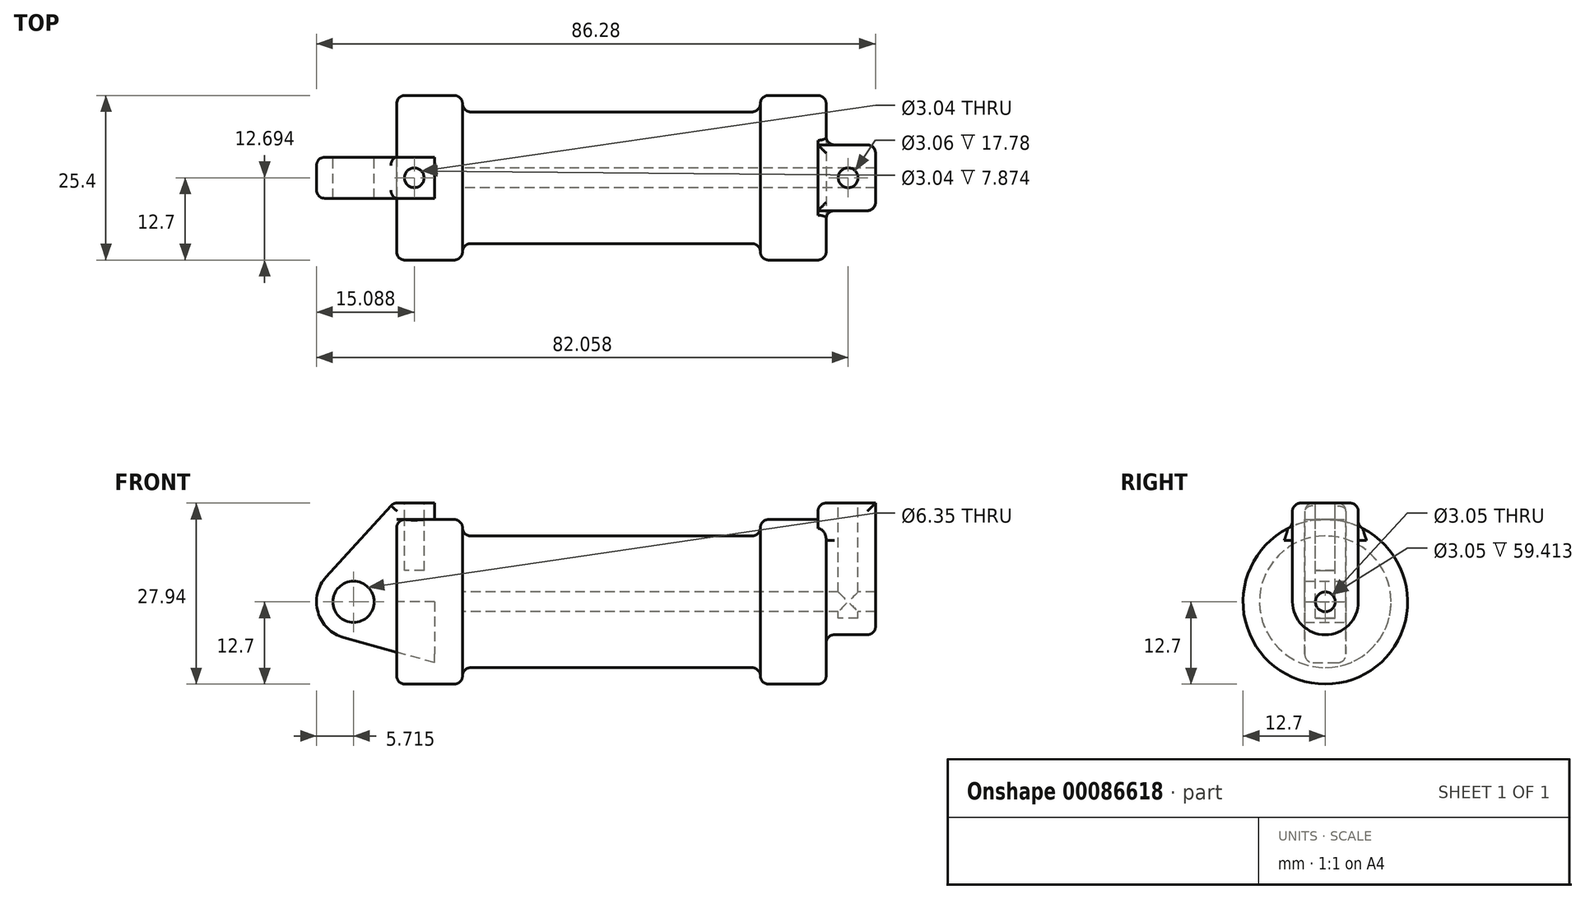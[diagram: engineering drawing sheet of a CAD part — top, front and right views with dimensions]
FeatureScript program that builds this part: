
annotation { "Feature Type Name" : "Feature", "Feature Type Description" : "" }
export const myFeature = defineFeature(function(context is Context, id is Id, definition is map)
    precondition{}
    {
        {
            var Q0;
            Q0=qCreatedBy(makeId("Front.planeOp"),FACE);
            var sketch = newSketch(context, id + "F0", { "sketchPlane" : qUnion([Q0])});
            skLineSegment(sketch, "E0", {"start": v(0, 0) * mm, "end": v(0, 12.7) * mm});
            skLineSegment(sketch, "E1", {"start": v(0, 12.7) * mm, "end": v(10.16, 12.7) * mm});
            skLineSegment(sketch, "E2", {"start": v(10.16, 12.7) * mm, "end": v(10.16, 10.16) * mm});
            skLineSegment(sketch, "E3", {"start": v(10.16, 10.16) * mm, "end": v(56.13, 10.16) * mm});
            skLineSegment(sketch, "E4", {"start": v(56.13, 10.16) * mm, "end": v(56.13, 12.7) * mm});
            skLineSegment(sketch, "E5", {"start": v(56.13, 12.7) * mm, "end": v(66.3, 12.7) * mm});
            skLineSegment(sketch, "E6", {"start": v(66.3, 12.7) * mm, "end": v(66.3, 0) * mm});
            skLineSegment(sketch, "E7", {"start": v(66.3, 0) * mm, "end": v(0, 0) * mm});
            skLineSegment(sketch, "E8", {"start": v(5.84, 15.24) * mm, "end": v(-0.5, 15.24) * mm});
            skLineSegment(sketch, "E9", {"start": v(-0.5, 15.24) * mm, "end": v(-10.88, 3.85) * mm});
            skLineSegment(sketch, "E10", {"start": v(0, 0) * mm, "end": v(-6.65, 0) * mm});
            skCircle(sketch, "E11", {"center": v(-6.65, 0) * mm, "radius": 5.72 * mm});
            skCircle(sketch, "E12", {"center": v(-6.65, 0) * mm, "radius": 3.18 * mm});
            skLineSegment(sketch, "E13", {"start": v(5.84, 15.24) * mm, "end": v(5.84, -9.4) * mm});
            skLineSegment(sketch, "E14", {"start": v(5.84, -9.4) * mm, "end": v(-8.18, -5.5) * mm});
            skSolve(sketch);
        }
        {
            var Q0;
            {var subQ0=sQuery(id+"F0.wireOp",EDGE,"E2");Q0=makeQuery(id+"F0.imprint","IMPRINT",FACE,{"disambiguationData":[TD([[makeQuery(id+"F0.imprint","IMPRINT",EDGE,{"derivedFrom":subQ0}),-1.0]])]});}
            var Q1;
            {var subQ0=sQuery(id+"F0.wireOp",EDGE,"E0");Q1=makeQuery(id+"F0.imprint","IMPRINT",FACE,{"disambiguationData":[TD([[makeQuery(id+"F0.imprint","IMPRINT",EDGE,{"derivedFrom":subQ0}),-1.0]])]});}
            var Q2;
            Q2=sQuery(id+"F0.wireOp",EDGE,"E7");
            revolve(context, id + "F1", {"entities" : qUnion([Q0, Q1]), "axis" : qUnion([Q2]), "revolveType" : RevolveType.FULL});
        }
        {
            var Q0;
            {var subQ3=sQuery(id+"F0.wireOp",EDGE,"E0");Q0=makeQuery(id+"F0.imprint","IMPRINT",FACE,{"disambiguationData":[TD([[makeQuery(id+"F0.imprint","IMPRINT",EDGE,{"derivedFrom":subQ3}),1.0]])]});}
            var Q1;
            {var subQ4=sQuery(id+"F0.wireOp",EDGE,"E12");Q1=makeQuery(id+"F0.imprint","IMPRINT",FACE,{"disambiguationData":[TD([[makeQuery(id+"F0.imprint","IMPRINT",EDGE,{"derivedFrom":subQ4}),-1.0]])]});}
            var Q2;
            {var subQ0=sQuery(id+"F0.wireOp",EDGE,"E14");Q2=makeQuery(id+"F0.imprint","IMPRINT",FACE,{"disambiguationData":[TD([[makeQuery(id+"F0.imprint","IMPRINT",EDGE,{"derivedFrom":subQ0}),-1.0]])]});}
            extrude(context, id + "F2", {"entities" : qUnion([Q0, Q1, Q2]), "endBound" : BoundingType.SYMMETRIC, "depth" : 6.35 * mm});
        }
        {
            var Q0;
            Q0=makeQuery(id+"F1.opRevolve","SWEPT_FACE",FACE,{"disambiguationData":[OSD([sQuery(id+"F0.wireOp",EDGE,"E6")])]});
            var sketch = newSketch(context, id + "F3", { "sketchPlane" : qUnion([Q0])});
            skCircle(sketch, "E15", {"center": v(0, 0) * mm, "radius": 1.52 * mm});
            skCircle(sketch, "E16", {"center": v(0, 0) * mm, "radius": 5.08 * mm});
            skLineSegment(sketch, "E17", {"start": v(-5.08, 0) * mm, "end": v(-5.08, 15.24) * mm});
            skLineSegment(sketch, "E18", {"start": v(5.08, 0) * mm, "end": v(5.08, 15.24) * mm});
            skLineSegment(sketch, "E19", {"start": v(-5.08, 15.24) * mm, "end": v(5.08, 15.24) * mm});
            skSolve(sketch);
        }
        {
            var Q0;
            {var subQ0=sQuery(id+"F3.wireOp",EDGE,"E17");var subQ1=sQuery(id+"F3.wireOp",EDGE,"E16");var subQ2=makeQuery(id+"F3.imprint","INTERSECT",VERTEX,{"derivedFrom":[subQ1,subQ0]});Q0=makeQuery(id+"F3.imprint","IMPRINT",FACE,{"disambiguationData":[TD([[makeQuery(id+"F3.imprint","IMPRINT",EDGE,{"disambiguationData":[TD([[subQ2,1.0]])],"derivedFrom":subQ1}),-1.0]])]});}
            var Q1;
            Q1=makeQuery(id+"F3.imprint","IMPRINT",FACE,{"disambiguationData":[TD([[makeQuery(id+"F3.imprint","IMPRINT",EDGE,{"derivedFrom":sQuery(id+"F3.wireOp",EDGE,"E15")}),-1.0]])]});
            var Q2;
            {var subQ0=sQuery(id+"F3.wireOp",EDGE,"E19");Q2=makeQuery(id+"F3.imprint","IMPRINT",FACE,{"disambiguationData":[TD([[makeQuery(id+"F3.imprint","IMPRINT",EDGE,{"derivedFrom":subQ0}),-1.0]])]});}
            extrude(context, id + "F4", {"entities" : qUnion([Q0, Q1, Q2]), "operationType" : NewBodyOperationType.ADD, "depth" : 7.62 * mm});
        }
        {
            var Q0;
            Q0=makeQuery(id+"F4.opExtrude","CAP_FACE",FACE,{"disambiguationData":[OSD([sQuery(id+"F3.wireOp",EDGE,"E15"),sQuery(id+"F3.wireOp",EDGE,"E16"),sQuery(id+"F3.wireOp",EDGE,"E17"),sQuery(id+"F3.wireOp",EDGE,"E18"),sQuery(id+"F3.wireOp",EDGE,"E19")])],"isStart":true});
            extrude(context, id + "F5", {"entities" : qUnion([Q0]), "operationType" : NewBodyOperationType.ADD, "depth" : 1.27 * mm});
        }
        {
            var Q0;
            Q0=makeQuery(id+"F4.opExtrude","CAP_FACE",FACE,{"disambiguationData":[OSD([sQuery(id+"F3.wireOp",EDGE,"E15"),sQuery(id+"F3.wireOp",EDGE,"E16"),sQuery(id+"F3.wireOp",EDGE,"E17"),sQuery(id+"F3.wireOp",EDGE,"E18"),sQuery(id+"F3.wireOp",EDGE,"E19")])],"isStart":false});
            var sketch = newSketch(context, id + "F6", { "sketchPlane" : qUnion([Q0])});
            skCircle(sketch, "E20", {"center": v(0, 0) * mm, "radius": 1.53 * mm});
            skSolve(sketch);
        }
        {
            var Q0;
            Q0=makeQuery(id+"F6.imprint","IMPRINT",FACE,{"disambiguationData":[TD([[makeQuery(id+"F6.imprint","IMPRINT",EDGE,{"derivedFrom":makeQuery(id+"F4.opExtrude","CAP_EDGE",EDGE,{"disambiguationData":[OSD([sQuery(id+"F3.wireOp",EDGE,"E15")])],"isStart":false})}),1.0]])]});
            var Q1;
            Q1=makeQuery(id+"F1.opRevolve","SWEPT_FACE",FACE,{"disambiguationData":[OSD([sQuery(id+"F0.wireOp",EDGE,"E2")])]});
            extrude(context, id + "F7", {"entities" : qUnion([Q0]), "operationType" : NewBodyOperationType.REMOVE, "endBound" : BoundingType.UP_TO_SURFACE, "oppositeDirection" : true, "endBoundEntityFace" : qUnion([Q1]), "depth" : 25.4 * mm});
        }
        {
            var Q0;
            Q0=makeQuery(id+"F2.opExtrude","SWEPT_FACE",FACE,{"disambiguationData":[OSD([sQuery(id+"F0.wireOp",EDGE,"E8")])]});
            var sketch = newSketch(context, id + "F8", { "sketchPlane" : qUnion([Q0])});
            skCircle(sketch, "E21", {"center": v(2.72, 0) * mm, "radius": 1.52 * mm});
            skCircle(sketch, "E22", {"center": v(69.69, 0) * mm, "radius": 1.53 * mm});
            skPoint(sketch, "E22.centerSnap0", {"position": v(5.84, 0) * mm});
            skSolve(sketch);
        }
        {
            var Q0;
            Q0=makeQuery(id+"F8.imprint","IMPRINT",FACE,{"disambiguationData":[TD([[makeQuery(id+"F8.imprint","IMPRINT",EDGE,{"derivedFrom":sQuery(id+"F8.wireOp",EDGE,"E22")}),1.0]])]});
            extrude(context, id + "F9", {"entities" : qUnion([Q0]), "operationType" : NewBodyOperationType.REMOVE, "oppositeDirection" : true, "depth" : 17.78 * mm});
        }
        {
            var Q0;
            Q0 = qSketchRegion(id + "F8", true);
            extrude(context, id + "F10", {"entities" : qUnion([Q0]), "operationType" : NewBodyOperationType.REMOVE, "oppositeDirection" : true, "depth" : 10.4 * mm});
        }
        {
            var Q0;
            Q0=makeQuery(id+"F1.opRevolve","SWEPT_FACE",FACE,{"disambiguationData":[OSD([sQuery(id+"F0.wireOp",EDGE,"E4")])]});
            var Q1;
            Q1=makeQuery(id+"F1.opRevolve","SWEPT_EDGE",EDGE,{"disambiguationData":[OSD([sQuery(id+"F0.wireOp",EDGE,"E0"),sQuery(id+"F0.wireOp",EDGE,"E1")])]});
            var Q2;
            Q2=makeQuery(id+"F1.opRevolve","SWEPT_FACE",FACE,{"disambiguationData":[OSD([sQuery(id+"F0.wireOp",EDGE,"E2")])]});
            var Q3;
            Q3=makeQuery(id+"F4.boolean.opBoolean","SPLIT",EDGE,{"disambiguationData":[OD(1.0)],"derivedFrom":makeQuery(id+"F1.opRevolve","SWEPT_EDGE",EDGE,{"disambiguationData":[OSD([sQuery(id+"F0.wireOp",EDGE,"E5"),sQuery(id+"F0.wireOp",EDGE,"E6")])]})});
            var Q4;
            Q4=makeQuery(id+"F2.opExtrude","CAP_EDGE",EDGE,{"disambiguationData":[OSD([sQuery(id+"F0.wireOp",EDGE,"E11")])],"isStart":false});
            var Q5;
            Q5=makeQuery(id+"F2.opExtrude","CAP_EDGE",EDGE,{"disambiguationData":[OSD([sQuery(id+"F0.wireOp",EDGE,"E14")])],"isStart":true});
            var Q6;
            Q6=makeQuery(id+"F4.opExtrude","CAP_EDGE",EDGE,{"disambiguationData":[OSD([sQuery(id+"F3.wireOp",EDGE,"E17")])],"isStart":false});
            var Q7;
            {var subQ0=sQuery(id+"F3.wireOp",EDGE,"E19");var subQ1=sQuery(id+"F3.wireOp",EDGE,"E17");Q7=makeQuery(id+"F5.boolean.opBoolean","MERGE",EDGE,{"derivedFrom":[makeQuery(id+"F4.opExtrude","SWEPT_EDGE",EDGE,{"disambiguationData":[OSD([subQ1,subQ0])]}),makeQuery(id+"F5.opExtrude","SWEPT_EDGE",EDGE,{"disambiguationData":[OSD([subQ1,subQ0])]})]});}
            var Q8;
            {var subQ0=sQuery(id+"F3.wireOp",EDGE,"E19");var subQ1=sQuery(id+"F3.wireOp",EDGE,"E18");Q8=makeQuery(id+"F5.boolean.opBoolean","MERGE",EDGE,{"derivedFrom":[makeQuery(id+"F4.opExtrude","SWEPT_EDGE",EDGE,{"disambiguationData":[OSD([subQ1,subQ0])]}),makeQuery(id+"F5.opExtrude","SWEPT_EDGE",EDGE,{"disambiguationData":[OSD([subQ1,subQ0])]})]});}
            var Q9;
            Q9=makeQuery(id+"F5.opExtrude","CAP_EDGE",EDGE,{"disambiguationData":[OSD([sQuery(id+"F3.wireOp",EDGE,"E19")])],"isStart":false});
            var Q10;
            Q10=makeQuery(id+"F5.opExtrude","CAP_EDGE",EDGE,{"disambiguationData":[OSD([sQuery(id+"F0.wireOp",EDGE,"E5"),sQuery(id+"F0.wireOp",EDGE,"E6")])],"isStart":false});
            fillet(context, id + "F11", {"entities" : qUnion([Q0, Q1, Q2, Q3, Q4, Q5, Q6, Q7, Q8, Q9, Q10]), "radius" : 1.27 * mm, "tangentPropagation" : true, "allowEdgeOverflow" : false});
        }
        {
            var Q0;
            Q0=makeQuery(id+"F2.opExtrude","CAP_EDGE",EDGE,{"disambiguationData":[OSD([sQuery(id+"F0.wireOp",EDGE,"E8")])],"isStart":true});
            fillet(context, id + "F12", {"entities" : qUnion([Q0]), "radius" : 1.27 * mm, "tangentPropagation" : true, "allowEdgeOverflow" : false});
        }
        {
            var Q0;
            {var subQ0=sQuery(id+"F3.wireOp",EDGE,"E16");var subQ1=sQuery(id+"F3.wireOp",EDGE,"E17");Q0=makeQuery(id+"F4.boolean.opBoolean","SPLIT",EDGE,{"disambiguationData":[TD([makeQuery(id+"F4.opExtrude","SWEPT_FACE",FACE,{"disambiguationData":[OSD([subQ0])]})])],"derivedFrom":makeQuery(id+"F4.opExtrude","CAP_EDGE",EDGE,{"disambiguationData":[OSD([subQ1])],"isStart":true})});}
            fillet(context, id + "F13", {"entities" : qUnion([Q0]), "radius" : 1.27 * mm, "tangentPropagation" : true, "allowEdgeOverflow" : false});
        }
    });
